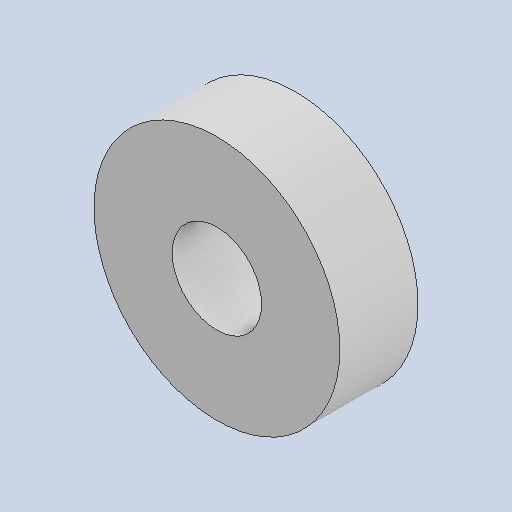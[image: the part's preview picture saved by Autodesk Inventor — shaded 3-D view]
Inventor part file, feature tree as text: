
AUTODESK INVENTOR PART (.ipt)
format: ipt  version: 2022 (Build 260153000, 153)  size: 93,184 bytes
history: native  units: in
note: dims shown in document units (in); Inventor stores cm internally (conversion verified against a paired STEP export)
features: other x3, sketch x1
ambient origin geometry x8: Origin, YZ Plane, XZ Plane, XY Plane, X Axis, Y Axis, Z Axis, Center Point
bodies: Solid1 (feature_tree)
feature tree (4):
  other  "608.ipt"
  other  "Solid1::608.ipt"
  other  "TaggingFeature1"
  sketch  "Sketch1"  dims[d0=0.3937in]
